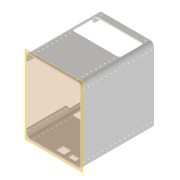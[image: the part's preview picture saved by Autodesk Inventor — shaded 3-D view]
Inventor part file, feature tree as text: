
AUTODESK INVENTOR PART (.ipt)
format: ipt  version: 2022 (Build 260153000, 153)  size: 385,536 bytes
history: native  units: mm
features: reference x10, sketch x6, projected_geometry x6, extrude x4, other x3, hole x2, fillet x2, plane x1, pattern_linear x1
ambient origin geometry x8: Origin, YZ Plane, XZ Plane, XY Plane, X Axis, Y Axis, Z Axis, Center Point
bodies: Volumenkörper1 (feature_tree)
feature tree (35):
  plane  "Arbeitsebene1"
  extrude  "Extrusion1"  Depth=3.0mm
  hole  "Bohrung1"  [1 undecoded]
  hole  "Bohrung2"  [1 undecoded]
  pattern_linear  "Rechteckige Anordnung1"  Spacing1=5.0mm  [1 undecoded]
  extrude  "Extrusion2"  TaperAngle=0.0deg  [1 undecoded]
  fillet  "Rundung1"  Radius=5.0mm
  extrude  "Extrusion3"  Depth=10.0mm TaperAngle=0.0deg
  fillet  "Rundung2"  [1 undecoded]
  extrude  "Extrusion4"  [1 undecoded]
  sketch  "Skizze1"  dims[d0=0.5mm d1=3.0mm]
  reference  "Referenz1"
  sketch  "Skizze2"  dims[d2=160.0mm d3=0.0mm]
  reference  "Referenz2"
  reference  "Referenz3"
  sketch  "Skizze3"  dims[d4=4.0mm d5=6.0mm d6=4.0mm d7=2.0mm d8=90.0deg d9=8.0mm d10=20.594885mm]
  reference  "Referenz4"
  reference  "Referenz5"
  sketch  "Skizze4"  dims[d11=4.0mm d12=6.0mm d13=4.0mm d14=2.0mm d15=90.0deg d16=8.0mm d17=20.594885mm d18=160.0mm d20=10.0mm]
  projected_geometry  "Projizierte Kontur1"
  projected_geometry  "Projizierte Kontur2"
  sketch  "Skizze5"  dims[d21=18.0mm d22=18.0mm]
  projected_geometry  "Projizierte Kontur3"
  projected_geometry  "Projizierte Kontur4"
  projected_geometry  "Projizierte Kontur5"
  projected_geometry  "Projizierte Kontur6"
  sketch  "Skizze6"  dims[d23=15.0mm d24=0.0mm d25=5.0mm d26=0.0mm d27=0.0mm d28=5.0mm d29=10.0mm d30=0.0mm]
  reference  "Referenz6"
  reference  "Referenz7"
  reference  "Referenz8"
  reference  "Referenz9"
  reference  "Referenz10"
  other  "Omnicscope_Xiao.iam"
  other  "Omniscope_USBC_Base:1"
  other  "00_Arduino_CNC_Assembly:1"
note: 6 required parameter values undecoded (feature->parameter linkage not recoverable at this tier; creation-order binding heuristic only, values carry confidence <= 0.55)
